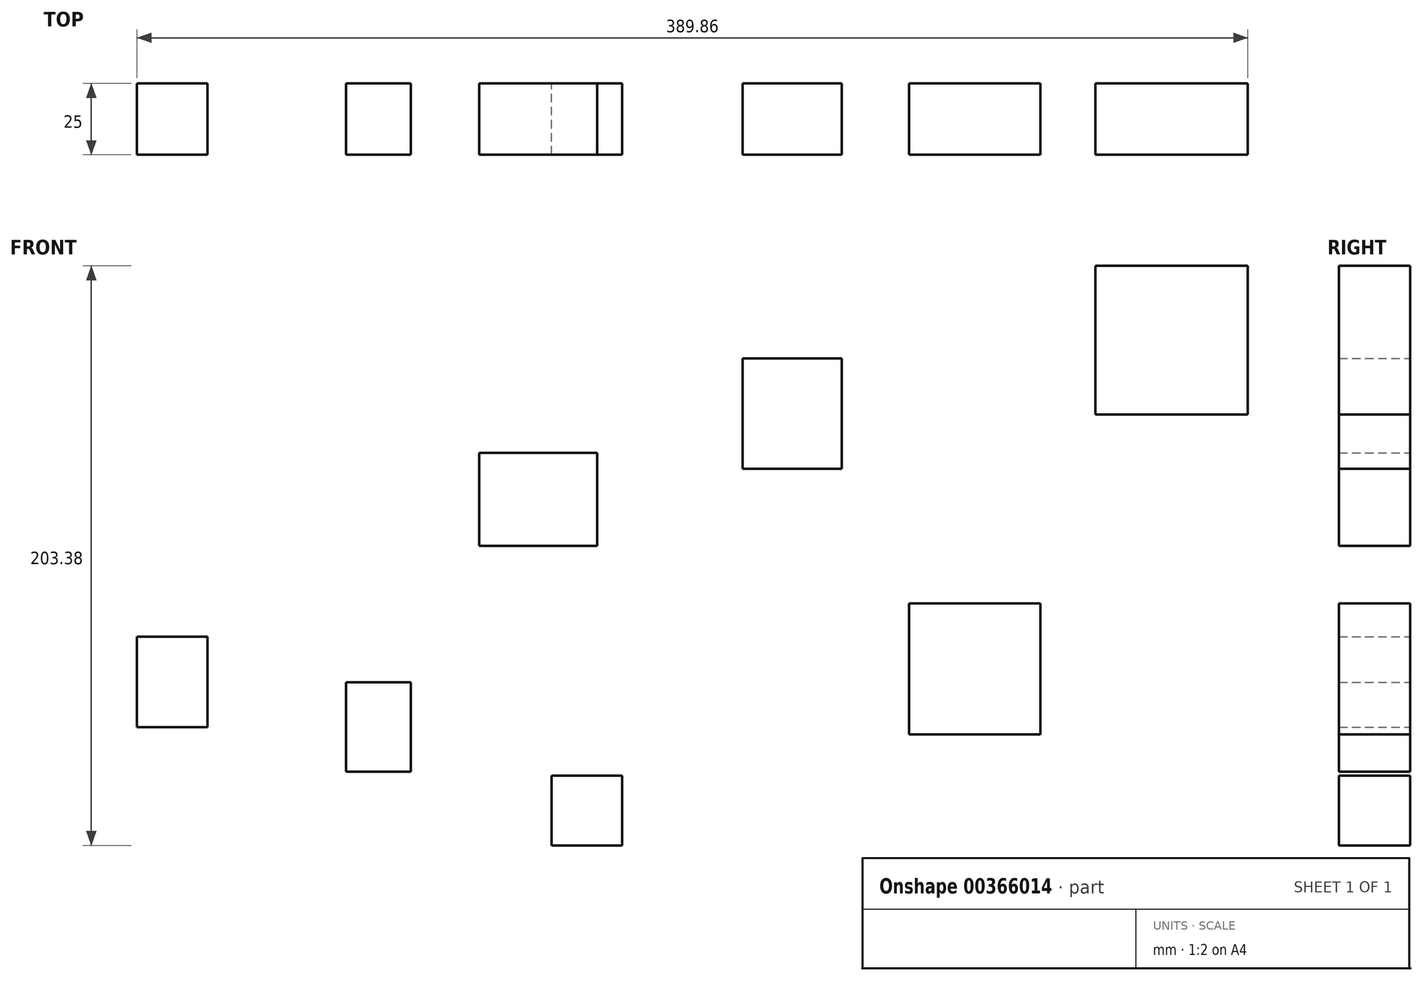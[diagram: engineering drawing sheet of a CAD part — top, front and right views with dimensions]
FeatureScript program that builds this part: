
annotation { "Feature Type Name" : "Feature", "Feature Type Description" : "" }
export const myFeature = defineFeature(function(context is Context, id is Id, definition is map)
    precondition{}
    {
        {
            var Q0;
            Q0=qCreatedBy(makeId("Front.planeOp"),FACE);
            var sketch = newSketch(context, id + "F0", { "sketchPlane" : qUnion([Q0])});
            skLineSegment(sketch, "E0.bottom", {"start": v(-89.12, 20.67) * mm, "end": v(-47.73, 20.67) * mm});
            skLineSegment(sketch, "E0.top", {"start": v(-89.12, 53.31) * mm, "end": v(-47.73, 53.31) * mm});
            skLineSegment(sketch, "E0.left", {"start": v(-89.12, 20.67) * mm, "end": v(-89.12, 53.31) * mm});
            skLineSegment(sketch, "E0.right", {"start": v(-47.73, 20.67) * mm, "end": v(-47.73, 53.31) * mm});
            skPoint(sketch, "E0.middle", {"position": v(-68.43, 37) * mm});
            skLineSegment(sketch, "E1.bottom", {"start": v(3.34, 47.7) * mm, "end": v(38.05, 47.7) * mm});
            skLineSegment(sketch, "E1.top", {"start": v(3.34, 86.42) * mm, "end": v(38.05, 86.42) * mm});
            skLineSegment(sketch, "E1.left", {"start": v(3.34, 47.7) * mm, "end": v(3.34, 86.42) * mm});
            skLineSegment(sketch, "E1.right", {"start": v(38.05, 47.7) * mm, "end": v(38.05, 86.42) * mm});
            skPoint(sketch, "E1.middle", {"position": v(20.7, 67.06) * mm});
            skLineSegment(sketch, "E2.bottom", {"start": v(127.17, 66.75) * mm, "end": v(180.58, 66.75) * mm});
            skLineSegment(sketch, "E2.top", {"start": v(127.17, 118.89) * mm, "end": v(180.58, 118.89) * mm});
            skLineSegment(sketch, "E2.left", {"start": v(127.17, 66.75) * mm, "end": v(127.17, 118.89) * mm});
            skLineSegment(sketch, "E2.right", {"start": v(180.58, 66.75) * mm, "end": v(180.58, 118.89) * mm});
            skPoint(sketch, "E2.middle", {"position": v(153.88, 92.82) * mm});
            skLineSegment(sketch, "E3.bottom", {"start": v(61.75, -45.6) * mm, "end": v(107.81, -45.6) * mm});
            skLineSegment(sketch, "E3.top", {"start": v(61.75, 0.41) * mm, "end": v(107.81, 0.41) * mm});
            skLineSegment(sketch, "E3.left", {"start": v(61.75, -45.6) * mm, "end": v(61.75, 0.41) * mm});
            skLineSegment(sketch, "E3.right", {"start": v(107.81, -45.6) * mm, "end": v(107.81, 0.41) * mm});
            skPoint(sketch, "E3.middle", {"position": v(84.78, -22.59) * mm});
            skSolve(sketch);
        }
        {
            var Q0;
            Q0=makeQuery(id+"F0.imprint","IMPRINT",FACE,{"disambiguationData":[TD([[makeQuery(id+"F0.imprint","IMPRINT",EDGE,{"derivedFrom":sQuery(id+"F0.wireOp",EDGE,"E0.bottom")}),1.0]])]});
            var Q1;
            Q1=makeQuery(id+"F0.imprint","IMPRINT",FACE,{"disambiguationData":[TD([[makeQuery(id+"F0.imprint","IMPRINT",EDGE,{"derivedFrom":sQuery(id+"F0.wireOp",EDGE,"E1.bottom")}),1.0]])]});
            var Q2;
            Q2=makeQuery(id+"F0.imprint","IMPRINT",FACE,{"disambiguationData":[TD([[makeQuery(id+"F0.imprint","IMPRINT",EDGE,{"derivedFrom":sQuery(id+"F0.wireOp",EDGE,"E2.bottom")}),1.0]])]});
            var Q3;
            Q3=makeQuery(id+"F0.imprint","IMPRINT",FACE,{"disambiguationData":[TD([[makeQuery(id+"F0.imprint","IMPRINT",EDGE,{"derivedFrom":sQuery(id+"F0.wireOp",EDGE,"E3.bottom")}),1.0]])]});
            extrude(context, id + "F1", {"entities" : qUnion([Q0, Q1, Q2, Q3]), "depth" : 25 * mm});
        }
        {
            var Q0;
            Q0=qCreatedBy(makeId("Front.planeOp"),FACE);
            var sketch = newSketch(context, id + "F2", { "sketchPlane" : qUnion([Q0])});
            skLineSegment(sketch, "E4.bottom", {"start": v(-209.28, -43.06) * mm, "end": v(-184.58, -43.06) * mm});
            skLineSegment(sketch, "E4.top", {"start": v(-209.28, -11.23) * mm, "end": v(-184.58, -11.23) * mm});
            skLineSegment(sketch, "E4.left", {"start": v(-209.28, -43.06) * mm, "end": v(-209.28, -11.23) * mm});
            skLineSegment(sketch, "E4.right", {"start": v(-184.58, -43.06) * mm, "end": v(-184.58, -11.23) * mm});
            skPoint(sketch, "E4.middle", {"position": v(-196.93, -27.14) * mm});
            skLineSegment(sketch, "E5.bottom", {"start": v(-135.85, -58.58) * mm, "end": v(-113.15, -58.58) * mm});
            skLineSegment(sketch, "E5.top", {"start": v(-135.85, -27.32) * mm, "end": v(-113.15, -27.32) * mm});
            skLineSegment(sketch, "E5.left", {"start": v(-135.85, -58.58) * mm, "end": v(-135.85, -27.32) * mm});
            skLineSegment(sketch, "E5.right", {"start": v(-113.15, -58.58) * mm, "end": v(-113.15, -27.32) * mm});
            skPoint(sketch, "E5.middle", {"position": v(-124.5, -42.95) * mm});
            skLineSegment(sketch, "E6.bottom", {"start": v(-63.75, -84.5) * mm, "end": v(-39.05, -84.5) * mm});
            skLineSegment(sketch, "E6.top", {"start": v(-63.75, -60) * mm, "end": v(-39.05, -60) * mm});
            skLineSegment(sketch, "E6.left", {"start": v(-63.75, -84.5) * mm, "end": v(-63.75, -60) * mm});
            skLineSegment(sketch, "E6.right", {"start": v(-39.05, -84.5) * mm, "end": v(-39.05, -60) * mm});
            skPoint(sketch, "E6.middle", {"position": v(-51.4, -72.25) * mm});
            skSolve(sketch);
        }
        {
            var Q0;
            Q0 = qSketchRegion(id + "F2", true);
            extrude(context, id + "F3", {"entities" : qUnion([Q0]), "depth" : 25 * mm});
        }
    });
